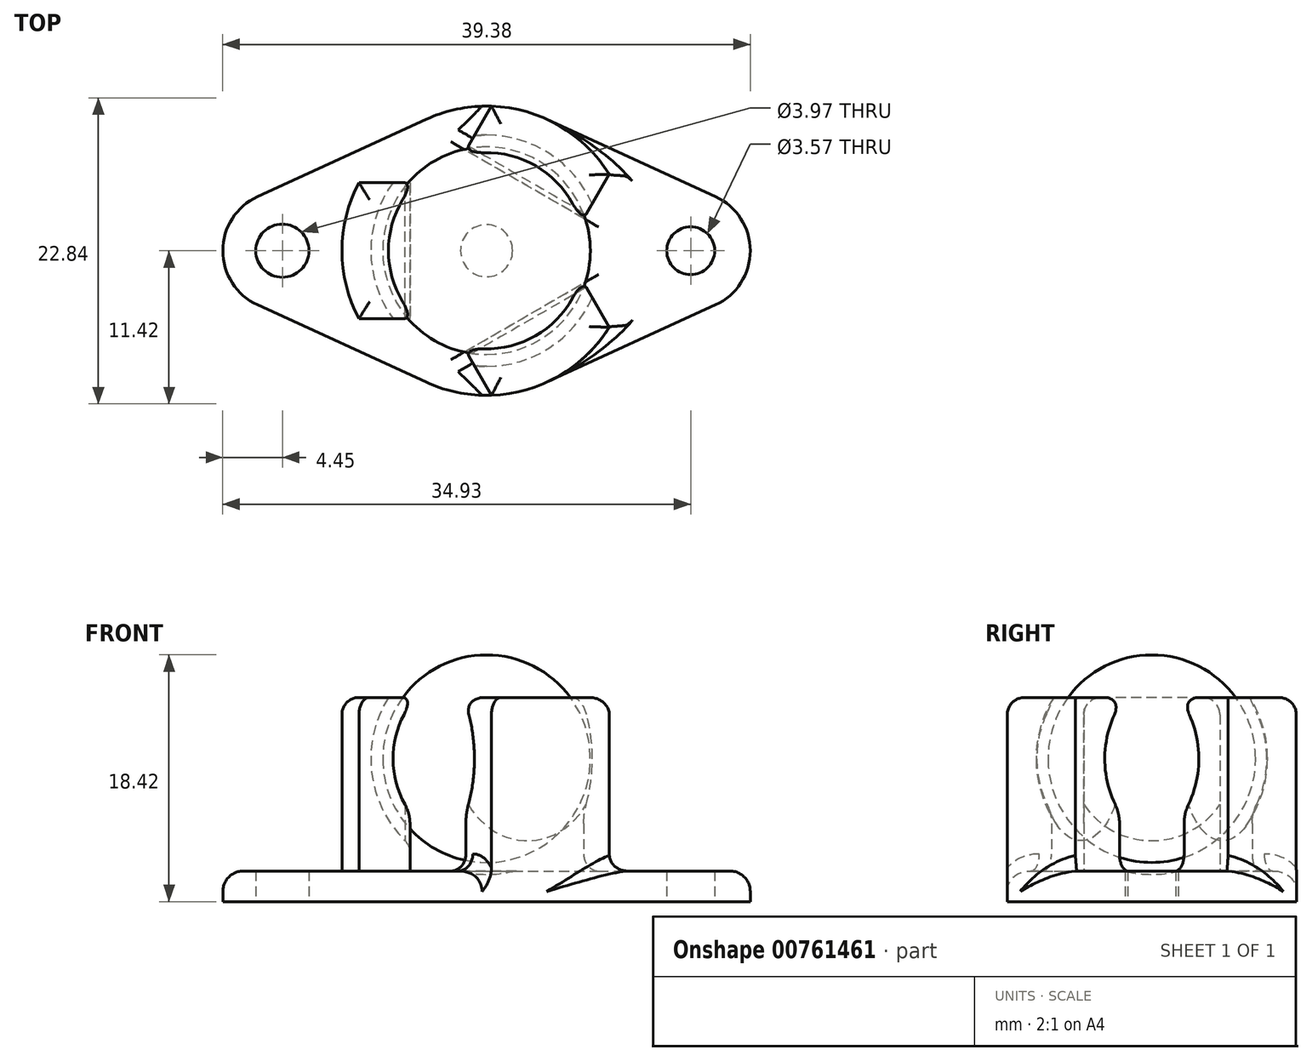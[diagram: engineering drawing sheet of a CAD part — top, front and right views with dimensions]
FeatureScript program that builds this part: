
annotation { "Feature Type Name" : "Feature", "Feature Type Description" : "" }
export const myFeature = defineFeature(function(context is Context, id is Id, definition is map)
    precondition{}
    {
        {
            var Q0;
            Q0=qCreatedBy(makeId("Top.planeOp"),FACE);
            var sketch = newSketch(context, id + "F0", { "sketchPlane" : qUnion([Q0])});
            skArc(sketch, "E0", {"start": v(2.04, 7.6) * mm, "mid": v(-7.6, 2.04) * mm, "end": v(-2.04, -7.6) * mm, "construction": true});
            skArc(sketch, "E1", {"start": v(10.8, 0) * mm, "mid": v(9.09, 5.83) * mm, "end": v(4.5, 9.81) * mm, "construction": true});
            skArc(sketch, "E2", {"start": v(-17.1, 4.04) * mm, "mid": v(-19.69, 0) * mm, "end": v(-17.1, -4.04) * mm});
            skArc(sketch, "E3", {"start": v(17.1, -4.04) * mm, "mid": v(19.69, 0) * mm, "end": v(17.1, 4.04) * mm});
            skLineSegment(sketch, "E4", {"start": v(17.1, -4.04) * mm, "end": v(4.5, -9.81) * mm});
            skLineSegment(sketch, "E5", {"start": v(-4.5, -9.81) * mm, "end": v(-17.1, -4.04) * mm});
            skLineSegment(sketch, "E6", {"start": v(-4.5, 9.81) * mm, "end": v(-17.1, 4.04) * mm});
            skLineSegment(sketch, "E7", {"start": v(17.1, 4.04) * mm, "end": v(4.5, 9.81) * mm});
            skCircle(sketch, "E8", {"center": v(15.24, 0) * mm, "radius": 1.79 * mm});
            skCircle(sketch, "E9", {"center": v(-15.24, 0) * mm, "radius": 1.98 * mm});
            skArc(sketch, "E10.trimOffspring", {"start": v(7.87, 0) * mm, "mid": v(6.25, 4.8) * mm, "end": v(2.04, 7.6) * mm, "construction": true});
            skArc(sketch, "E11.trimOffspring", {"start": v(-2.04, -7.6) * mm, "mid": v(4.8, -6.25) * mm, "end": v(7.87, 0) * mm, "construction": true});
            skArc(sketch, "E12.trimOffspring", {"start": v(-4.5, -9.81) * mm, "mid": v(0, -10.8) * mm, "end": v(4.5, -9.81) * mm});
            skPoint(sketch, "E13.start.orphan", {"position": v(0, 10.8) * mm});
            skLineSegment(sketch, "E14.bottom", {"start": v(-9.53, -5.08) * mm, "end": v(-5.71, -5.08) * mm});
            skLineSegment(sketch, "E14.right", {"start": v(-5.71, -5.08) * mm, "end": v(-5.71, 5.08) * mm});
            skArc(sketch, "E15", {"start": v(4.5, -9.81) * mm, "mid": v(9.09, -5.83) * mm, "end": v(10.8, 0) * mm, "construction": true});
            skArc(sketch, "E16", {"start": v(-4.5, 9.81) * mm, "mid": v(-7.4, 7.86) * mm, "end": v(-9.53, 5.08) * mm, "construction": true});
            skArc(sketch, "E17", {"start": v(4.5, 9.81) * mm, "mid": v(0, 10.8) * mm, "end": v(-4.5, 9.81) * mm});
            skArc(sketch, "E18", {"start": v(-9.53, 5.08) * mm, "mid": v(-10.8, 0) * mm, "end": v(-9.53, -5.08) * mm});
            skArc(sketch, "E19", {"start": v(-9.53, -5.08) * mm, "mid": v(-7.4, -7.86) * mm, "end": v(-4.5, -9.81) * mm, "construction": true});
            skLineSegment(sketch, "E20", {"start": v(-5.71, 5.08) * mm, "end": v(-9.53, 5.08) * mm});
            skArc(sketch, "E21.1.0", {"start": v(0.36, -10.79) * mm, "mid": v(5.4, -9.35) * mm, "end": v(9.16, -5.7) * mm});
            skLineSegment(sketch, "E21.1.1", {"start": v(-1.54, -7.49) * mm, "end": v(0.36, -10.79) * mm});
            skLineSegment(sketch, "E21.1.2", {"start": v(7.26, -2.4) * mm, "end": v(-1.54, -7.49) * mm});
            skLineSegment(sketch, "E21.1.3", {"start": v(9.16, -5.7) * mm, "end": v(7.26, -2.4) * mm});
            skArc(sketch, "E21.2.0", {"start": v(9.16, 5.7) * mm, "mid": v(5.4, 9.35) * mm, "end": v(0.36, 10.79) * mm});
            skLineSegment(sketch, "E21.2.1", {"start": v(7.26, 2.4) * mm, "end": v(9.16, 5.7) * mm});
            skLineSegment(sketch, "E21.2.2", {"start": v(-1.54, 7.49) * mm, "end": v(7.26, 2.4) * mm});
            skLineSegment(sketch, "E21.2.3", {"start": v(0.36, 10.79) * mm, "end": v(-1.54, 7.49) * mm});
            skSolve(sketch);
        }
        {
            var Q0;
            Q0 = qSketchRegion(id + "F0", true);
            var Q1;
            Q1=makeQuery(id+"F0.imprint","IMPRINT",FACE,{"disambiguationData":[TD([[makeQuery(id+"F0.imprint","IMPRINT",EDGE,{"derivedFrom":sQuery(id+"F0.wireOp",EDGE,"gm98KNGP-oXZy-XAed-11qp-XDqhcD0MRLNN")}),1.0]])]});
            var Q2;
            Q2=makeQuery(id+"F0.imprint","IMPRINT",FACE,{"disambiguationData":[TD([[makeQuery(id+"F0.imprint","IMPRINT",EDGE,{"derivedFrom":sQuery(id+"F0.wireOp",EDGE,"gm98KNGP-oXZy-XAed-11qp-XDqhcD0MRLNN")}),-1.0]])]});
            extrude(context, id + "F1", {"entities" : qUnion([Q0, Q1, Q2]), "depth" : 2.3 * mm, "offsetDistance" : 25.4 * mm});
        }
        {
            var Q0;
            Q0=makeQuery(id+"F0.imprint","IMPRINT",FACE,{"disambiguationData":[TD([[makeQuery(id+"F0.imprint","IMPRINT",EDGE,{"derivedFrom":sQuery(id+"F0.wireOp",EDGE,"E14.bottom")}),1.0]])]});
            var Q1;
            {var subQ0=sQuery(id+"F0.wireOp",EDGE,"E21.1.1");Q1=makeQuery(id+"F0.imprint","IMPRINT",FACE,{"disambiguationData":[TD([[makeQuery(id+"F0.imprint","IMPRINT",EDGE,{"derivedFrom":subQ0}),1.0]])]});}
            var Q2;
            {var subQ0=sQuery(id+"F0.wireOp",EDGE,"E21.2.1");Q2=makeQuery(id+"F0.imprint","IMPRINT",FACE,{"disambiguationData":[TD([[makeQuery(id+"F0.imprint","IMPRINT",EDGE,{"derivedFrom":subQ0}),1.0]])]});}
            extrude(context, id + "F2", {"entities" : qUnion([Q0, Q1, Q2]), "operationType" : NewBodyOperationType.ADD, "depth" : 15.24 * mm, "offsetDistance" : 25.4 * mm});
        }
        {
            var Q0;
            Q0=qCreatedBy(makeId("Top.planeOp"),FACE);
            var sketch = newSketch(context, id + "F3", { "sketchPlane" : qUnion([Q0])});
            skLineSegment(sketch, "E22.0", {"start": v(0, 7.75) * mm, "end": v(0, -7.75) * mm});
            skArc(sketch, "E22.1", {"start": v(0, -7.75) * mm, "mid": v(7.75, 0) * mm, "end": v(0, 7.75) * mm});
            skSolve(sketch);
        }
        {
            var Q0;
            Q0=makeQuery(id+"F3.imprint","IMPRINT",FACE,{"disambiguationData":[TD([[makeQuery(id+"F3.imprint","IMPRINT",EDGE,{"derivedFrom":sQuery(id+"F3.wireOp",EDGE,"E22.0")}),1.0]])]});
            var Q1;
            Q1=sQuery(id+"F3.wireOp",EDGE,"E22.0");
            revolve(context, id + "F4", {"surfaceOperationType" : NewSurfaceOperationType.NEW, "entities" : qUnion([Q0]), "axis" : qUnion([Q1]), "revolveType" : RevolveType.FULL});
        }
        {
            var Q0;
            Q0=makeQuery(id+"F4.opRevolve","SWEPT_BODY",BODY,{"disambiguationData":[OSD([sQuery(id+"F3.wireOp",EDGE,"E22.0"),sQuery(id+"F3.wireOp",EDGE,"E22.1")])]});
            transform(context, id + "F5", {"entities" : qUnion([Q0]), "transformType" : TransformType.TRANSLATION_3D, "dx" : 0 * mm, "dy" : 0 * mm, "dz" : 10.67 * mm, "makeCopy" : false});
        }
        {
            var Q0;
            Q0=makeQuery(id+"F4.opRevolve","SWEPT_BODY",BODY,{"disambiguationData":[OSD([sQuery(id+"F3.wireOp",EDGE,"E22.0"),sQuery(id+"F3.wireOp",EDGE,"E22.1")])]});
            var Q1;
            Q1=makeQuery(id+"F1.opExtrude","SWEPT_BODY",BODY,{"disambiguationData":[OSD([sQuery(id+"F0.wireOp",EDGE,"E2"),sQuery(id+"F0.wireOp",EDGE,"E3"),sQuery(id+"F0.wireOp",EDGE,"E4"),sQuery(id+"F0.wireOp",EDGE,"E5"),sQuery(id+"F0.wireOp",EDGE,"E6"),sQuery(id+"F0.wireOp",EDGE,"E7"),sQuery(id+"F0.wireOp",EDGE,"E8"),sQuery(id+"F0.wireOp",EDGE,"E9"),sQuery(id+"F0.wireOp",EDGE,"E12.trimOffspring"),sQuery(id+"F0.wireOp",EDGE,"E14.bottom"),sQuery(id+"F0.wireOp",EDGE,"E14.right"),sQuery(id+"F0.wireOp",EDGE,"E17"),sQuery(id+"F0.wireOp",EDGE,"E18"),sQuery(id+"F0.wireOp",EDGE,"E20"),sQuery(id+"F0.wireOp",EDGE,"E21.1.0"),sQuery(id+"F0.wireOp",EDGE,"E21.2.0")])]});
            var Q2;
            Q2=makeQuery(id+"F4.opRevolve","SWEPT_FACE",FACE,{"disambiguationData":[OSD([sQuery(id+"F3.wireOp",EDGE,"E22.1")])]});
            booleanBodies(context, id + "F6", {"operationType" : BooleanOperationType.SUBTRACTION, "tools" : qUnion([Q0]), "targets" : qUnion([Q1]), "offset" : true, "entitiesToOffset" : qUnion([Q2]), "offsetDistance" : 0.89 * mm, "keepTools" : true});
        }
        {
            var Q0;
            Q0=makeQuery(id+"F1.opExtrude","CAP_EDGE",EDGE,{"disambiguationData":[OSD([sQuery(id+"F0.wireOp",EDGE,"E7")])],"isStart":false});
            var Q1;
            Q1=makeQuery(id+"F1.opExtrude","CAP_EDGE",EDGE,{"disambiguationData":[OSD([sQuery(id+"F0.wireOp",EDGE,"E5")])],"isStart":false});
            fillet(context, id + "F7", {"entities" : qUnion([Q0, Q1]), "radius" : 1.52 * mm, "tangentPropagation" : true, "allowEdgeOverflow" : false});
        }
        {
            var Q0;
            Q0=makeQuery(id+"F2.boolean.opBoolean","INTERSECT",EDGE,{"derivedFrom":[makeQuery(id+"F1.opExtrude","CAP_FACE",FACE,{"disambiguationData":[OSD([sQuery(id+"F0.wireOp",EDGE,"E2"),sQuery(id+"F0.wireOp",EDGE,"E3"),sQuery(id+"F0.wireOp",EDGE,"E4"),sQuery(id+"F0.wireOp",EDGE,"E5"),sQuery(id+"F0.wireOp",EDGE,"E6"),sQuery(id+"F0.wireOp",EDGE,"E7"),sQuery(id+"F0.wireOp",EDGE,"E8"),sQuery(id+"F0.wireOp",EDGE,"E9"),sQuery(id+"F0.wireOp",EDGE,"E12.trimOffspring"),sQuery(id+"F0.wireOp",EDGE,"E14.bottom"),sQuery(id+"F0.wireOp",EDGE,"E14.right"),sQuery(id+"F0.wireOp",EDGE,"E17"),sQuery(id+"F0.wireOp",EDGE,"E18"),sQuery(id+"F0.wireOp",EDGE,"E20"),sQuery(id+"F0.wireOp",EDGE,"E21.1.0"),sQuery(id+"F0.wireOp",EDGE,"E21.2.0")])],"isStart":false}),makeQuery(id+"F2.opExtrude","SWEPT_FACE",FACE,{"disambiguationData":[OSD([sQuery(id+"F0.wireOp",EDGE,"E21.1.3")])]})]});
            var Q1;
            Q1=makeQuery(id+"F2.boolean.opBoolean","INTERSECT",EDGE,{"derivedFrom":[makeQuery(id+"F1.opExtrude","CAP_FACE",FACE,{"disambiguationData":[OSD([sQuery(id+"F0.wireOp",EDGE,"E2"),sQuery(id+"F0.wireOp",EDGE,"E3"),sQuery(id+"F0.wireOp",EDGE,"E4"),sQuery(id+"F0.wireOp",EDGE,"E5"),sQuery(id+"F0.wireOp",EDGE,"E6"),sQuery(id+"F0.wireOp",EDGE,"E7"),sQuery(id+"F0.wireOp",EDGE,"E8"),sQuery(id+"F0.wireOp",EDGE,"E9"),sQuery(id+"F0.wireOp",EDGE,"E12.trimOffspring"),sQuery(id+"F0.wireOp",EDGE,"E14.bottom"),sQuery(id+"F0.wireOp",EDGE,"E14.right"),sQuery(id+"F0.wireOp",EDGE,"E17"),sQuery(id+"F0.wireOp",EDGE,"E18"),sQuery(id+"F0.wireOp",EDGE,"E20"),sQuery(id+"F0.wireOp",EDGE,"E21.1.0"),sQuery(id+"F0.wireOp",EDGE,"E21.2.0")])],"isStart":false}),makeQuery(id+"F2.opExtrude","SWEPT_FACE",FACE,{"disambiguationData":[OSD([sQuery(id+"F0.wireOp",EDGE,"E21.2.1")])]})]});
            var Q2;
            {var subQ0=sQuery(id+"F0.wireOp",EDGE,"E21.2.0");Q2=makeQuery(id+"F7.opFillet","BLEND_EDGE",EDGE,{"blendedFrom":[makeQuery(id+"F1.opExtrude","CAP_EDGE",EDGE,{"disambiguationData":[OSD([sQuery(id+"F0.wireOp",EDGE,"E7")])],"isStart":false}),makeQuery(id+"F2.boolean.opBoolean","MERGE",FACE,{"derivedFrom":[makeQuery(id+"F1.opExtrude","SWEPT_FACE",FACE,{"disambiguationData":[OSD([sQuery(id+"F0.wireOp",EDGE,"E17"),subQ0])]}),makeQuery(id+"F2.opExtrude","SWEPT_FACE",FACE,{"disambiguationData":[OSD([subQ0])]})]})],"blendedInto":[makeQuery(id+"F2.boolean.opBoolean","MERGE",FACE,{"derivedFrom":[makeQuery(id+"F1.opExtrude","SWEPT_FACE",FACE,{"disambiguationData":[OSD([sQuery(id+"F0.wireOp",EDGE,"E17"),subQ0])]}),makeQuery(id+"F2.opExtrude","SWEPT_FACE",FACE,{"disambiguationData":[OSD([subQ0])]})]})]});}
            var Q3;
            Q3=makeQuery(id+"F7.opFillet","BLEND_EDGE",EDGE,{"blendedFrom":[makeQuery(id+"F1.opExtrude","CAP_EDGE",EDGE,{"disambiguationData":[OSD([sQuery(id+"F0.wireOp",EDGE,"E17"),sQuery(id+"F0.wireOp",EDGE,"E21.2.0")])],"isStart":false}),makeQuery(id+"F2.opExtrude","SWEPT_FACE",FACE,{"disambiguationData":[OSD([sQuery(id+"F0.wireOp",EDGE,"E21.2.3")])]})],"blendedInto":[makeQuery(id+"F2.opExtrude","SWEPT_FACE",FACE,{"disambiguationData":[OSD([sQuery(id+"F0.wireOp",EDGE,"E21.2.3")])]})]});
            var Q4;
            Q4=makeQuery(id+"F1.opExtrude","CAP_EDGE",EDGE,{"disambiguationData":[OSD([sQuery(id+"F0.wireOp",EDGE,"E20")])],"isStart":false});
            var Q5;
            Q5=makeQuery(id+"F1.opExtrude","CAP_EDGE",EDGE,{"disambiguationData":[OSD([sQuery(id+"F0.wireOp",EDGE,"E18")])],"isStart":false});
            var Q6;
            Q6=makeQuery(id+"F1.opExtrude","CAP_EDGE",EDGE,{"disambiguationData":[OSD([sQuery(id+"F0.wireOp",EDGE,"E14.bottom")])],"isStart":false});
            var Q7;
            Q7=makeQuery(id+"F7.opFillet","BLEND_EDGE",EDGE,{"blendedFrom":[makeQuery(id+"F1.opExtrude","CAP_EDGE",EDGE,{"disambiguationData":[OSD([sQuery(id+"F0.wireOp",EDGE,"E12.trimOffspring"),sQuery(id+"F0.wireOp",EDGE,"E21.1.0")])],"isStart":false}),makeQuery(id+"F2.opExtrude","SWEPT_FACE",FACE,{"disambiguationData":[OSD([sQuery(id+"F0.wireOp",EDGE,"E21.1.1")])]})],"blendedInto":[makeQuery(id+"F2.opExtrude","SWEPT_FACE",FACE,{"disambiguationData":[OSD([sQuery(id+"F0.wireOp",EDGE,"E21.1.1")])]})]});
            var Q8;
            Q8=makeQuery(id+"F7.opFillet","BLEND_EDGE",EDGE,{"blendedFrom":[makeQuery(id+"F1.opExtrude","CAP_EDGE",EDGE,{"disambiguationData":[OSD([sQuery(id+"F0.wireOp",EDGE,"E5")])],"isStart":false}),makeQuery(id+"F2.opExtrude","SWEPT_FACE",FACE,{"disambiguationData":[OSD([sQuery(id+"F0.wireOp",EDGE,"E21.1.1")])]})],"blendedInto":[makeQuery(id+"F2.opExtrude","SWEPT_FACE",FACE,{"disambiguationData":[OSD([sQuery(id+"F0.wireOp",EDGE,"E21.1.1")])]})]});
            var Q9;
            {var subQ0=sQuery(id+"F0.wireOp",EDGE,"E21.1.0");Q9=makeQuery(id+"F7.opFillet","BLEND_EDGE",EDGE,{"blendedFrom":[makeQuery(id+"F1.opExtrude","CAP_EDGE",EDGE,{"disambiguationData":[OSD([sQuery(id+"F0.wireOp",EDGE,"E4")])],"isStart":false}),makeQuery(id+"F2.boolean.opBoolean","MERGE",FACE,{"derivedFrom":[makeQuery(id+"F1.opExtrude","SWEPT_FACE",FACE,{"disambiguationData":[OSD([sQuery(id+"F0.wireOp",EDGE,"E12.trimOffspring"),subQ0])]}),makeQuery(id+"F2.opExtrude","SWEPT_FACE",FACE,{"disambiguationData":[OSD([subQ0])]})]})],"blendedInto":[makeQuery(id+"F2.boolean.opBoolean","MERGE",FACE,{"derivedFrom":[makeQuery(id+"F1.opExtrude","SWEPT_FACE",FACE,{"disambiguationData":[OSD([sQuery(id+"F0.wireOp",EDGE,"E12.trimOffspring"),subQ0])]}),makeQuery(id+"F2.opExtrude","SWEPT_FACE",FACE,{"disambiguationData":[OSD([subQ0])]})]})]});}
            var Q10;
            Q10=makeQuery(id+"F2.opExtrude","CAP_EDGE",EDGE,{"disambiguationData":[OSD([sQuery(id+"F0.wireOp",EDGE,"E14.bottom")])],"isStart":false});
            var Q11;
            Q11=makeQuery(id+"F2.opExtrude","CAP_EDGE",EDGE,{"disambiguationData":[OSD([sQuery(id+"F0.wireOp",EDGE,"E18")])],"isStart":false});
            var Q12;
            Q12=makeQuery(id+"F2.opExtrude","CAP_EDGE",EDGE,{"disambiguationData":[OSD([sQuery(id+"F0.wireOp",EDGE,"E20")])],"isStart":false});
            var Q13;
            Q13=makeQuery(id+"F2.opExtrude","CAP_EDGE",EDGE,{"disambiguationData":[OSD([sQuery(id+"F0.wireOp",EDGE,"E21.1.3")])],"isStart":false});
            var Q14;
            Q14=makeQuery(id+"F2.opExtrude","CAP_EDGE",EDGE,{"disambiguationData":[OSD([sQuery(id+"F0.wireOp",EDGE,"E21.1.0")])],"isStart":false});
            var Q15;
            Q15=makeQuery(id+"F2.opExtrude","CAP_EDGE",EDGE,{"disambiguationData":[OSD([sQuery(id+"F0.wireOp",EDGE,"E21.1.1")])],"isStart":false});
            var Q16;
            Q16=makeQuery(id+"F2.opExtrude","CAP_EDGE",EDGE,{"disambiguationData":[OSD([sQuery(id+"F0.wireOp",EDGE,"E21.2.1")])],"isStart":false});
            var Q17;
            Q17=makeQuery(id+"F2.opExtrude","CAP_EDGE",EDGE,{"disambiguationData":[OSD([sQuery(id+"F0.wireOp",EDGE,"E21.2.0")])],"isStart":false});
            var Q18;
            Q18=makeQuery(id+"F2.opExtrude","CAP_EDGE",EDGE,{"disambiguationData":[OSD([sQuery(id+"F0.wireOp",EDGE,"E21.2.3")])],"isStart":false});
            fillet(context, id + "F8", {"entities" : qUnion([Q0, Q1, Q2, Q3, Q4, Q5, Q6, Q7, Q8, Q9, Q10, Q11, Q12, Q13, Q14, Q15, Q16, Q17, Q18]), "radius" : 1.27 * mm, "tangentPropagation" : true, "allowEdgeOverflow" : false});
        }
        {
            var Q0;
            Q0=makeQuery(id+"F6.tempBoolean.opBoolean","INTERSECT",EDGE,{"disambiguationData":[OD(2.0)],"derivedFrom":[makeQuery(id+"F2.opExtrude","SWEPT_FACE",FACE,{"disambiguationData":[OSD([sQuery(id+"F0.wireOp",EDGE,"E14.right")])]}),makeQuery(id+"F6.offsetTempBody.opPattern","COPY",FACE,{"derivedFrom":makeQuery(id+"F4.opRevolve","SWEPT_FACE",FACE,{"disambiguationData":[OSD([sQuery(id+"F3.wireOp",EDGE,"E22.1")])]}),"instanceName":"1"})]});
            var Q1;
            Q1=makeQuery(id+"F6.tempBoolean.opBoolean","INTERSECT",EDGE,{"disambiguationData":[OD(2.0)],"derivedFrom":[makeQuery(id+"F2.opExtrude","SWEPT_FACE",FACE,{"disambiguationData":[OSD([sQuery(id+"F0.wireOp",EDGE,"E21.2.2")])]}),makeQuery(id+"F6.offsetTempBody.opPattern","COPY",FACE,{"derivedFrom":makeQuery(id+"F4.opRevolve","SWEPT_FACE",FACE,{"disambiguationData":[OSD([sQuery(id+"F3.wireOp",EDGE,"E22.1")])]}),"instanceName":"1"})]});
            var Q2;
            Q2=makeQuery(id+"F6.tempBoolean.opBoolean","INTERSECT",EDGE,{"disambiguationData":[OD(2.0)],"derivedFrom":[makeQuery(id+"F2.opExtrude","SWEPT_FACE",FACE,{"disambiguationData":[OSD([sQuery(id+"F0.wireOp",EDGE,"E21.1.2")])]}),makeQuery(id+"F6.offsetTempBody.opPattern","COPY",FACE,{"derivedFrom":makeQuery(id+"F4.opRevolve","SWEPT_FACE",FACE,{"disambiguationData":[OSD([sQuery(id+"F3.wireOp",EDGE,"E22.1")])]}),"instanceName":"1"})]});
            var Q3;
            Q3=makeQuery(id+"F6.tempBoolean.opBoolean","COPY",FACE,{"disambiguationData":[TD([makeQuery(id+"F1.opExtrude","CAP_FACE",FACE,{"disambiguationData":[OSD([sQuery(id+"F0.wireOp",EDGE,"E2"),sQuery(id+"F0.wireOp",EDGE,"E3"),sQuery(id+"F0.wireOp",EDGE,"E4"),sQuery(id+"F0.wireOp",EDGE,"E5"),sQuery(id+"F0.wireOp",EDGE,"E6"),sQuery(id+"F0.wireOp",EDGE,"E7"),sQuery(id+"F0.wireOp",EDGE,"E8"),sQuery(id+"F0.wireOp",EDGE,"E9"),sQuery(id+"F0.wireOp",EDGE,"E12.trimOffspring"),sQuery(id+"F0.wireOp",EDGE,"E14.bottom"),sQuery(id+"F0.wireOp",EDGE,"E14.right"),sQuery(id+"F0.wireOp",EDGE,"E17"),sQuery(id+"F0.wireOp",EDGE,"E18"),sQuery(id+"F0.wireOp",EDGE,"E20"),sQuery(id+"F0.wireOp",EDGE,"E21.1.0"),sQuery(id+"F0.wireOp",EDGE,"E21.2.0")])],"isStart":false})])],"derivedFrom":makeQuery(id+"F6.offsetTempBody.opPattern","COPY",FACE,{"derivedFrom":makeQuery(id+"F4.opRevolve","SWEPT_FACE",FACE,{"disambiguationData":[OSD([sQuery(id+"F3.wireOp",EDGE,"E22.1")])]}),"instanceName":"1"})});
            fillet(context, id + "F9", {"entities" : qUnion([Q0, Q1, Q2, Q3]), "radius" : 1.27 * mm, "tangentPropagation" : true, "allowEdgeOverflow" : false});
        }
    });
